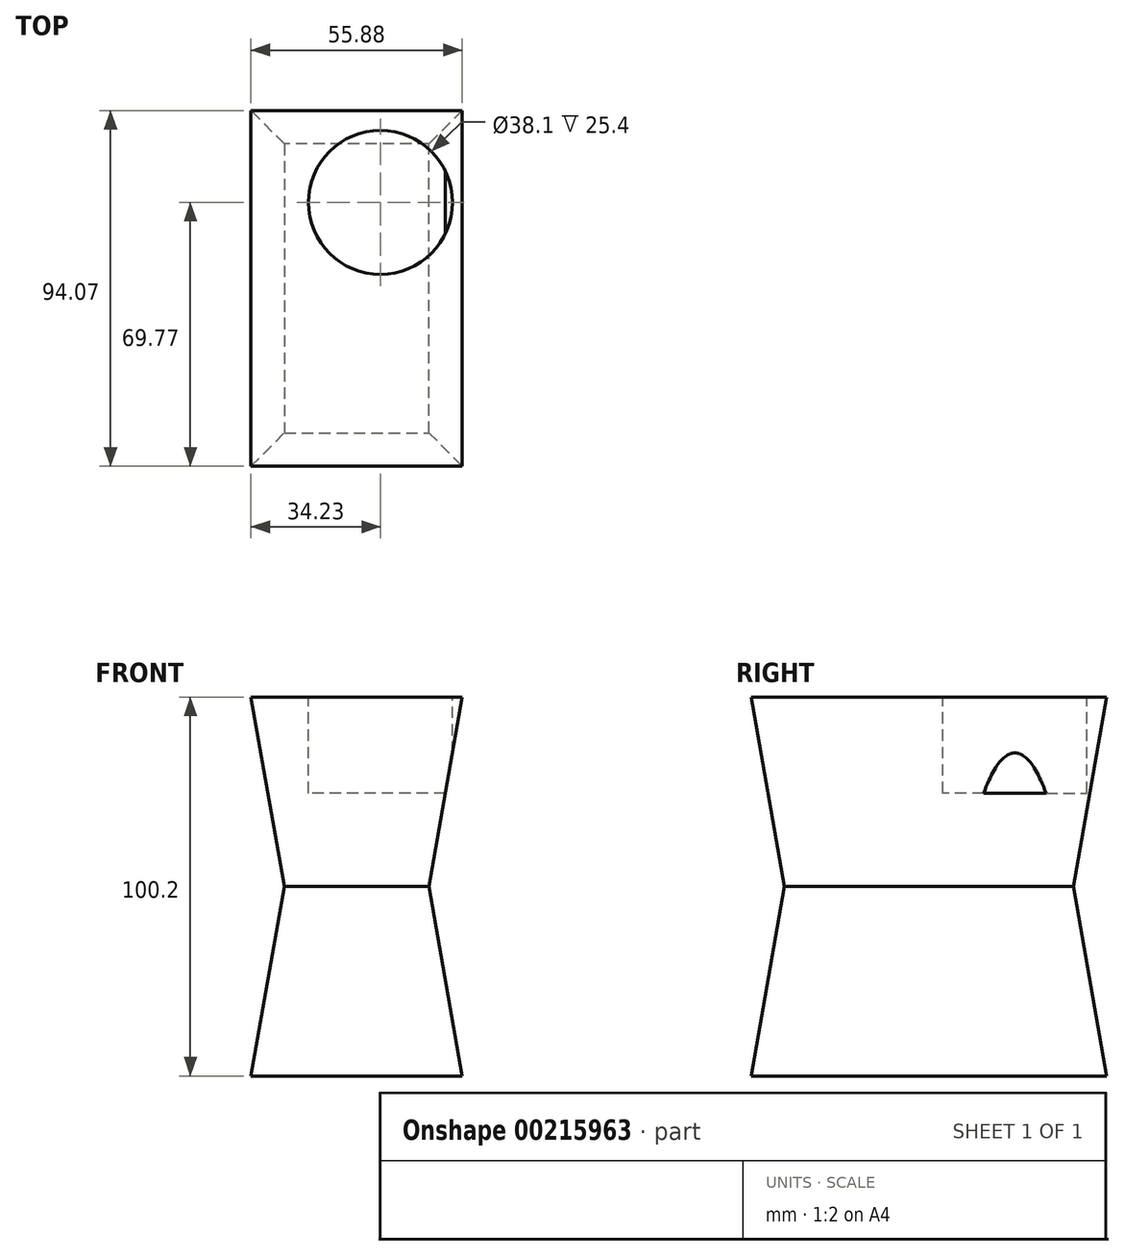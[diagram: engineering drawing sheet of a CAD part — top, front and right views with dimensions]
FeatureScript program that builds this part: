
annotation { "Feature Type Name" : "Feature", "Feature Type Description" : "" }
export const myFeature = defineFeature(function(context is Context, id is Id, definition is map)
    precondition{}
    {
        {
            var Q0;
            Q0=qCreatedBy(makeId("Top.planeOp"),FACE);
            var sketch = newSketch(context, id + "F0", { "sketchPlane" : qUnion([Q0])});
            skLineSegment(sketch, "E0.bottom", {"start": v(0, -60.94) * mm, "end": v(38.22, -60.94) * mm});
            skLineSegment(sketch, "E0.top", {"start": v(0, 15.47) * mm, "end": v(38.22, 15.47) * mm});
            skLineSegment(sketch, "E0.left", {"start": v(0, 15.47) * mm, "end": v(0, -60.94) * mm});
            skLineSegment(sketch, "E0.right", {"start": v(38.22, 15.47) * mm, "end": v(38.22, -60.94) * mm});
            skSolve(sketch);
        }
        {
            var Q0;
            Q0 = qSketchRegion(id + "F0", true);
            extrude(context, id + "F1", {"entities" : qUnion([Q0]), "endBound" : BoundingType.SYMMETRIC, "oppositeDirection" : true, "depth" : 100.2 * mm, "hasDraft" : true, "draftAngle" : 10 * degree});
        }
        {
            var Q0;
            Q0=makeQuery(id+"F1.opExtrude","CAP_FACE",FACE,{"disambiguationData":[OSD([sQuery(id+"F0.wireOp",EDGE,"E0.bottom"),sQuery(id+"F0.wireOp",EDGE,"E0.top"),sQuery(id+"F0.wireOp",EDGE,"E0.left"),sQuery(id+"F0.wireOp",EDGE,"E0.right")])],"isStart":true});
            var sketch = newSketch(context, id + "F2", { "sketchPlane" : qUnion([Q0])});
            skCircle(sketch, "E1", {"center": v(25.4, 0) * mm, "radius": 19.05 * mm});
            skSolve(sketch);
        }
        {
            var Q0;
            Q0 = qSketchRegion(id + "F2", true);
            extrude(context, id + "F3", {"entities" : qUnion([Q0]), "operationType" : NewBodyOperationType.REMOVE, "oppositeDirection" : true, "depth" : 25.4 * mm});
        }
    });
